# Revit family: Zumtobel ECOOS2
name_source: partatom
category: Lighting Fixtures
revit_build: Autodesk Revit 2016 (Build: 20150220_1215(x64)
units: mm (PartAtom-declared; Revit-internal decimal feet)

## family parameters
Cut with Voids When Loaded = No
Host = Face
Light Source = Yes
OmniClass Number = 23.80.70.11
OmniClass Title = Luminaries for Internal Lighting
Part Type = Normal
Room Calculation Point = No
Round Connector Dimension = Use Diameter
Shared = No

## types (4) — shared parameters
Assembly Code = D5020200
Body = ZG_Metal_Light_Grey
Color Filter = 16777215
Cover = ZG_PMMA_Opaque
Dimming Lamp Color Temperature Shift = <None>
Emit Shape Visible in Rendering = No
Emit from Rectangle Length = 120 mm  [stored 0.393701 ft]
Height = 76 mm  [stored 0.249344 ft]
Lamp = LED
Manufacturer = Zumtobel Lighting
Tilt Angle = -90.00°
Voltage = 230 V
Width = 120 mm  [stored 0.393701 ft]
zero-valued in all types: Default Elevation

## per-type parameters (varying)
| type | Apparent Load | Description | Emit from Rectangle Width | Length | Model | No TEC Track Mount | Photometric Web File | TEC Track Mount | URL |
| ECOOS2 4400 L12 | 37 VA | Surface mount or pendant LED luminaire | 1251 mm  [stored 4.10433 ft] | 1264 mm | 42186821 | No | 42186821_(STD_LEO).IES | Yes | www.zumtobel.com/42186821 |
| ECOOS2 5500 L15 | 47 VA | Surface mount or pendant LED luminaire | 1499 mm  [stored 4.91798 ft] | 1512 mm  [stored 4.96063 ft] | 42186823 | Yes | 42186823_(STD_LEO).IES | No | www.zumtobel.de/42186823 |
| ECOOS2 4400 TEC L12 | 37 VA | TECTON track mount LED luminaire | 1251 mm  [stored 4.10433 ft] | 1264 mm | 42932536 | No | 42932536_(STD_LEO).IES | Yes | www.zumtobel.com/42932536 |
| ECOOS2 5500 TEC L15 | 47 VA | TECTON track mount LED luminaire | 1499 mm  [stored 4.91798 ft] | 1512 mm  [stored 4.96063 ft] | 42932538 | No | 42932538_(STD_LEO).IES | Yes | www.zumtobel.de/42932538 |

note: [stored X ft] marks values corroborated as IEEE doubles in the binary element streams (Revit-internal decimal feet)

## geometry (parser evidence)
native form markers: Blend x2, Sweep x7
no freeform markers — native parametric forms only
